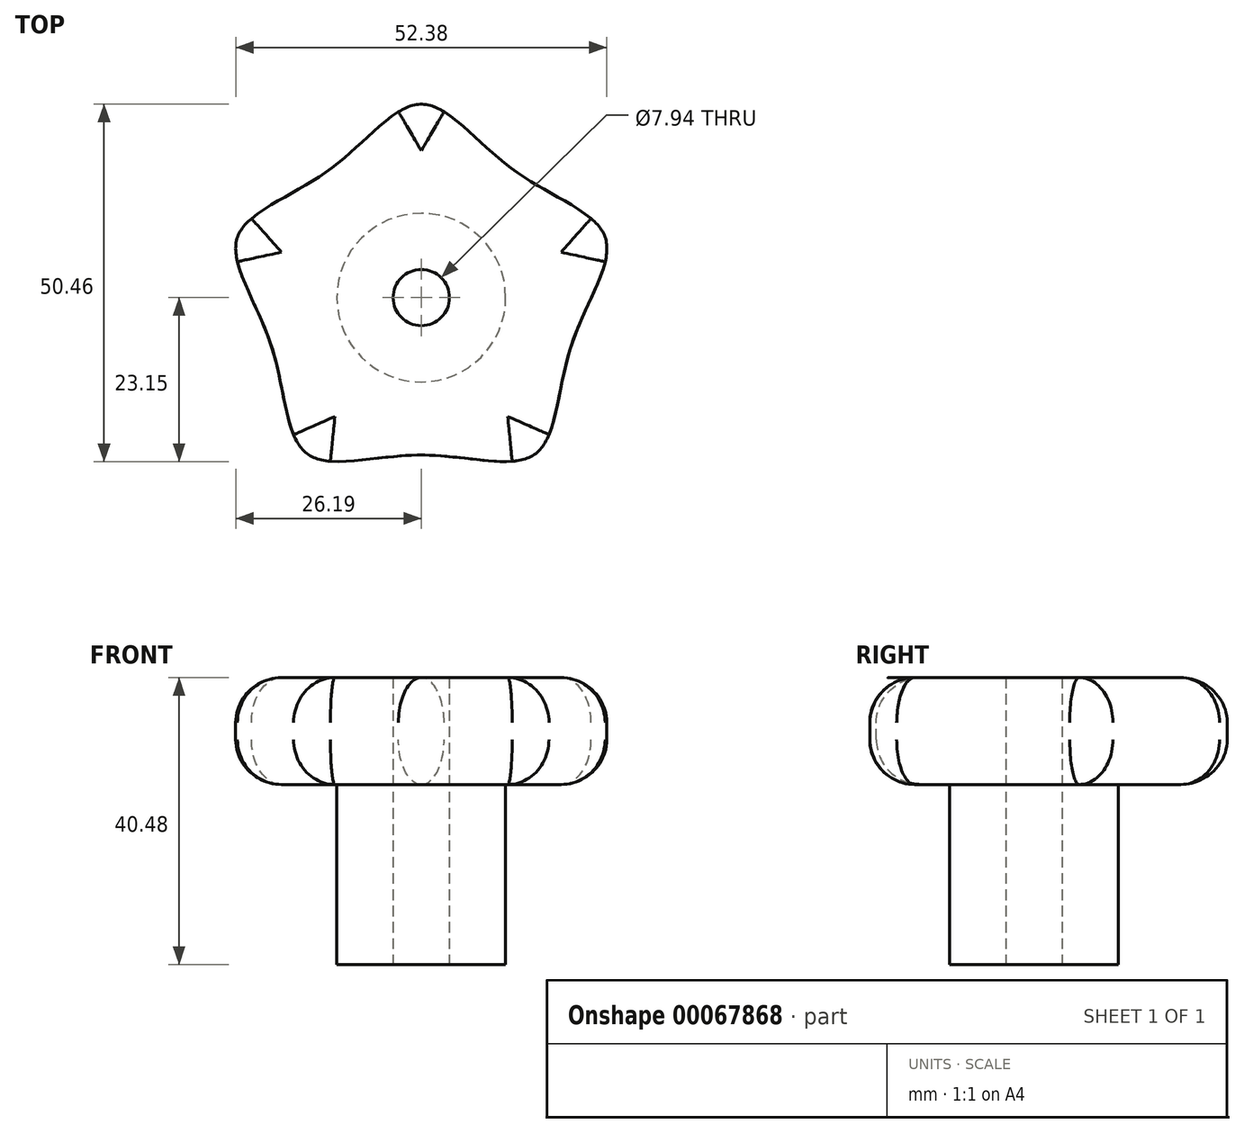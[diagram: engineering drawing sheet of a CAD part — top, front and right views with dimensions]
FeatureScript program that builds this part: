
annotation { "Feature Type Name" : "Feature", "Feature Type Description" : "" }
export const myFeature = defineFeature(function(context is Context, id is Id, definition is map)
    precondition{}
    {
        {
            var Q0;
            Q0=qCreatedBy(makeId("Front.planeOp"),FACE);
            var sketch = newSketch(context, id + "F0", { "sketchPlane" : qUnion([Q0])});
            skLineSegment(sketch, "E0", {"start": v(0, -80.95) * mm, "end": v(0, 138.65) * mm, "construction": true});
            skLineSegment(sketch, "E1.bottom", {"start": v(3.97, 40.48) * mm, "end": v(27.78, 40.48) * mm});
            skLineSegment(sketch, "E1.top", {"start": v(11.9, 25.4) * mm, "end": v(27.78, 25.4) * mm});
            skLineSegment(sketch, "E1.right", {"start": v(27.78, 40.48) * mm, "end": v(27.78, 25.4) * mm});
            skLineSegment(sketch, "E2.top", {"start": v(3.97, 0) * mm, "end": v(11.9, 0) * mm});
            skLineSegment(sketch, "E2.left", {"start": v(3.97, 40.48) * mm, "end": v(3.97, 0) * mm});
            skLineSegment(sketch, "E2.right", {"start": v(11.9, 25.4) * mm, "end": v(11.9, 0) * mm});
            skSolve(sketch);
        }
        {
            var Q0;
            Q0=makeQuery(id+"F0.imprint","IMPRINT",FACE,{"disambiguationData":[TD([[makeQuery(id+"F0.imprint","IMPRINT",EDGE,{"derivedFrom":sQuery(id+"F0.wireOp",EDGE,"c77c49e3-3ca0-4727-9ada-1d302668ea3e")}),-1.0]])]});
            var Q1;
            Q1=makeQuery(id+"F0.imprint","IMPRINT",FACE,{"disambiguationData":[TD([[makeQuery(id+"F0.imprint","IMPRINT",EDGE,{"derivedFrom":sQuery(id+"F0.wireOp",EDGE,"E1.bottom")}),-1.0]])]});
            var Q2;
            Q2=sQuery(id+"F0.wireOp",EDGE,"E0");
            revolve(context, id + "F3", {"entities" : qUnion([Q0, Q1]), "axis" : qUnion([Q2]), "revolveType" : RevolveType.FULL});
        }
        {
            var Q0;
            Q0=makeQuery(id+"F3.opRevolve","SWEPT_FACE",FACE,{"disambiguationData":[OSD([sQuery(id+"F0.wireOp",EDGE,"E1.bottom")])]});
            var sketch = newSketch(context, id + "F1", { "sketchPlane" : qUnion([Q0])});
            skFitSpline(sketch, "E3", {"points": [v(0, 27.3) * mm, v(13.06, 17.98) * mm, v(25.97, 8.44) * mm, v(21.14, -6.87) * mm, v(16.05, -22.1) * mm, v(0, -22.23) * mm, v(-16.05, -22.1) * mm, v(-21.14, -6.87) * mm, v(-25.97, 8.44) * mm, v(-13.06, 17.98) * mm, v(0, 27.3) * mm]});
            skCircle(sketch, "E4", {"center": v(0, 0) * mm, "radius": 27.3 * mm, "construction": true});
            skLineSegment(sketch, "E5", {"start": v(0, 0) * mm, "end": v(0, 27.3) * mm, "construction": true});
            skLineSegment(sketch, "E6", {"start": v(0, 0) * mm, "end": v(25.97, 8.44) * mm, "construction": true});
            skLineSegment(sketch, "E7", {"start": v(0, 0) * mm, "end": v(16.05, -22.1) * mm, "construction": true});
            skLineSegment(sketch, "E8", {"start": v(0, 0) * mm, "end": v(-13.06, 17.98) * mm, "construction": true});
            skLineSegment(sketch, "E9", {"start": v(0, 0) * mm, "end": v(-21.14, -6.87) * mm, "construction": true});
            skCircle(sketch, "E10", {"center": v(0, 0) * mm, "radius": 22.23 * mm, "construction": true});
            skCircle(sketch, "E11.0", {"center": v(0, 0) * mm, "radius": 27.78 * mm});
            skSolve(sketch);
        }
        {
            var Q0;
            Q0=makeQuery(id+"F1.imprint","IMPRINT",FACE,{"disambiguationData":[TD([[makeQuery(id+"F1.imprint","IMPRINT",EDGE,{"derivedFrom":sQuery(id+"F1.wireOp",EDGE,"E3")}),1.0]])]});
            extrude(context, id + "F4", {"entities" : qUnion([Q0]), "operationType" : NewBodyOperationType.REMOVE, "endBound" : BoundingType.THROUGH_ALL, "depth" : 25.4 * mm, "hasSecondDirection" : true, "secondDirectionBound" : SecondDirectionBoundingType.THROUGH_ALL, "secondDirectionOppositeDirection" : true, "secondDirectionDepth" : 25.4 * mm});
        }
        {
            var Q0;
            Q0=makeQuery(id+"F4.boolean.opBoolean","COPY",FACE,{"derivedFrom":makeQuery(id+"F4.opExtrude","SWEPT_FACE",FACE,{"disambiguationData":[OSD([sQuery(id+"F1.wireOp",EDGE,"E3")])]})});
            fillet(context, id + "F2", {"entities" : qUnion([Q0]), "radius" : 6.35 * mm, "tangentPropagation" : true, "allowEdgeOverflow" : false});
        }
    });
